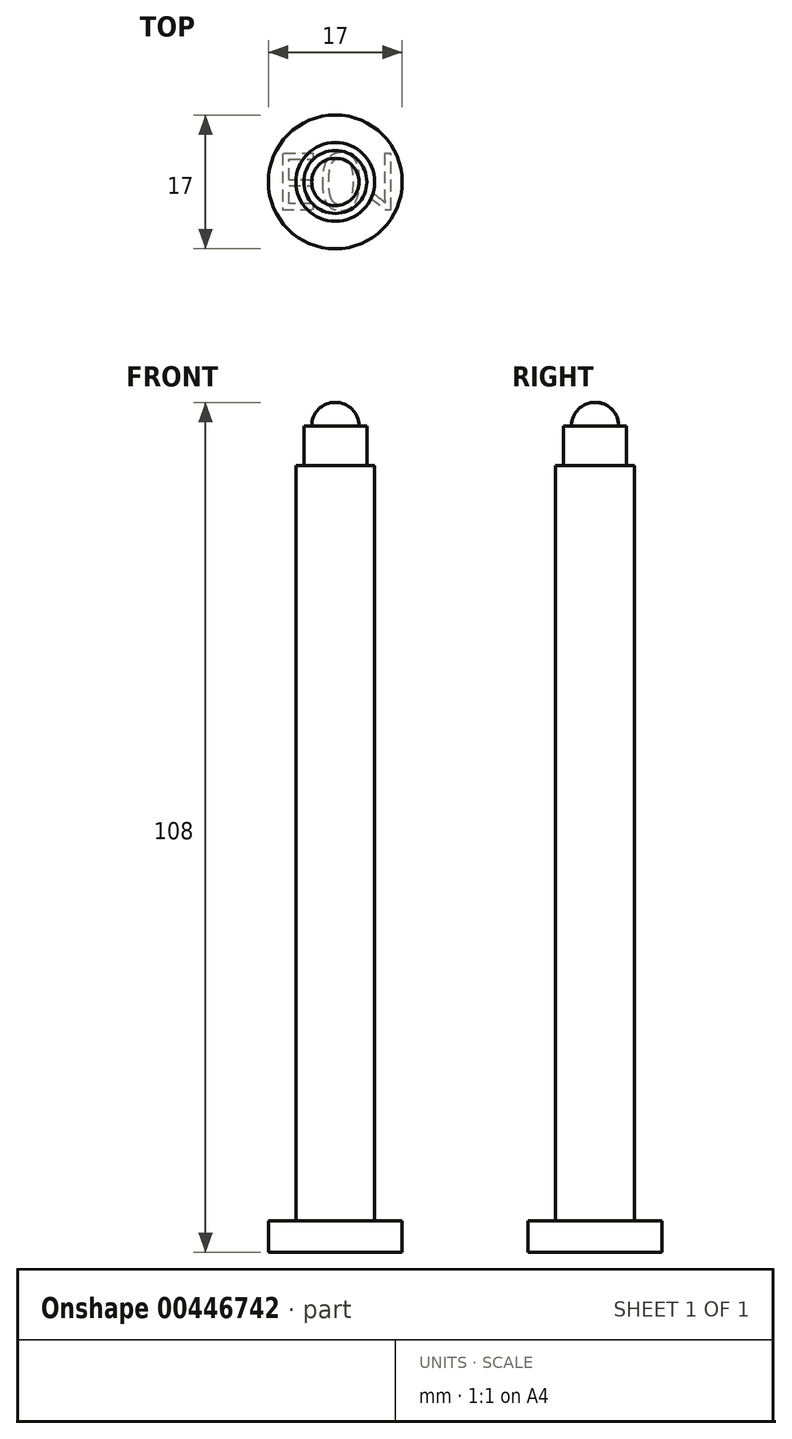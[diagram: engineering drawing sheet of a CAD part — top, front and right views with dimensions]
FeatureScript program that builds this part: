
annotation { "Feature Type Name" : "Feature", "Feature Type Description" : "" }
export const myFeature = defineFeature(function(context is Context, id is Id, definition is map)
    precondition{}
    {
        {
            var Q0;
            Q0=qCreatedBy(makeId("Top.planeOp"),FACE);
            var sketch = newSketch(context, id + "F0", { "sketchPlane" : qUnion([Q0])});
            skCircle(sketch, "E0", {"center": v(0, 0) * mm, "radius": 8.5 * mm});
            skSolve(sketch);
        }
        {
            var Q0;
            Q0=qSketchRegion(id+"F0",true);
            extrude(context, id + "F1", {"entities" : qUnion([Q0]), "depth" : 4 * mm});
        }
        {
            var Q0;
            Q0=qCreatedBy(makeId("Top.planeOp"),FACE);
            var sketch = newSketch(context, id + "F2", { "sketchPlane" : qUnion([Q0])});
            skCircle(sketch, "E1", {"center": v(0, 0) * mm, "radius": 5 * mm});
            skSolve(sketch);
        }
        {
            var Q0;
            Q0=qSketchRegion(id+"F2",true);
            extrude(context, id + "F3", {"entities" : qUnion([Q0]), "operationType" : NewBodyOperationType.ADD, "depth" : 100 * mm});
        }
        {
            var Q0;
            Q0=qCreatedBy(makeId("Right.planeOp"),FACE);
            var sketch = newSketch(context, id + "F4", { "sketchPlane" : qUnion([Q0])});
            skLineSegment(sketch, "E2", {"start": v(0, 105) * mm, "end": v(0, 100) * mm});
            skLineSegment(sketch, "E3", {"start": v(0, 100) * mm, "end": v(4, 100) * mm});
            skLineSegment(sketch, "E4", {"start": v(4, 100) * mm, "end": v(4, 105) * mm});
            skLineSegment(sketch, "E5", {"start": v(4, 105) * mm, "end": v(0, 105) * mm});
            skSolve(sketch);
        }
        {
            var Q0;
            Q0=makeQuery(id+"F4.imprint","IMPRINT",FACE,{"disambiguationData":[TD([[makeQuery(id+"F4.imprint","IMPRINT",EDGE,{"derivedFrom":sQuery(id+"F4.wireOp",EDGE,"E2")}),1.0]])]});
            var Q1;
            Q1=sQuery(id+"F4.wireOp",EDGE,"E2");
            revolve(context, id + "F5", {"operationType" : NewBodyOperationType.ADD, "entities" : qUnion([Q0]), "axis" : qUnion([Q1]), "revolveType" : RevolveType.FULL});
        }
        {
            var Q0;
            Q0=qCreatedBy(makeId("Right.planeOp"),FACE);
            var sketch = newSketch(context, id + "F6", { "sketchPlane" : qUnion([Q0])});
            skLineSegment(sketch, "E6", {"start": v(0, 108) * mm, "end": v(0, 105) * mm});
            skLineSegment(sketch, "E7", {"start": v(0, 105) * mm, "end": v(3, 105) * mm});
            skArc(sketch, "E8", {"start": v(3, 105) * mm, "mid": v(2.12, 107.12) * mm, "end": v(0, 108) * mm});
            skSolve(sketch);
        }
        {
            var Q0;
            Q0=makeQuery(id+"F6.imprint","IMPRINT",FACE,{"disambiguationData":[TD([[makeQuery(id+"F6.imprint","IMPRINT",EDGE,{"derivedFrom":sQuery(id+"F6.wireOp",EDGE,"E6")}),1.0]])]});
            var Q1;
            Q1=sQuery(id+"F6.wireOp",EDGE,"E6");
            revolve(context, id + "F7", {"operationType" : NewBodyOperationType.ADD, "entities" : qUnion([Q0]), "axis" : qUnion([Q1]), "revolveType" : RevolveType.FULL});
        }
        {
            var Q0;
            Q0=makeQuery(id+"F1.opExtrude","CAP_FACE",FACE,{"disambiguationData":[OSD([sQuery(id+"F0.wireOp",EDGE,"E0")])],"isStart":true});
            var sketch = newSketch(context, id + "F8", { "sketchPlane" : qUnion([Q0])});
            skText(sketch, "E9", { "text": "E01", "fontName": "OpenSans-Regular.ttf"});
            const initialGuessF8  = {"E9": [-0.00771, -0.00362, 1, 0, 0.0072]};
            skSetInitialGuess(sketch, initialGuessF8);
            skSolve(sketch);
        }
        {
            var Q0;
            Q0 = qSketchRegion(id + "F8", true);
            extrude(context, id + "F9", {"entities" : qUnion([Q0]), "operationType" : NewBodyOperationType.REMOVE, "oppositeDirection" : true, "depth" : 0.1 * mm, "offsetDistance" : 25 * mm});
        }
    });
